# Revit family: 1001R
name_source: partatom
category: Plumbing Fixtures
revit_build: Autodesk Revit 2018 (Build: 20170223_1515(x64)
units: mm (PartAtom-declared; Revit-internal decimal feet)

## family parameters
Cut with Voids When Loaded = No
Host = Face
OmniClass Number = 23.45.05.21.11.11
OmniClass Title = Water Operated Water Closets
Part Type = Normal
Room Calculation Point = No
Round Connector Dimension = Use Diameter
Shared = Yes

## types (1)
- 1001R
    1001R Rear-Mounted Toilet, Wall Supply = Yes
    Amperage = 0
    Assembly Code = D2010110
    CW Connection = Yes
    CWFU = 10
    Default Elevation = 15"
    Description = Wall Hung Toilet, Rear Mount
    EG Enviro-Glaze (for color selection see flier) = No
    HW Connection = Yes
    HWFU = 0
    Inlet Water Diameter = 1 1/2"
    Inlet Water Radius = 3/4"
    Installation Type = Wall Mounted
    Length = 24 1/4"
    Manufacturer = Murdock
    Material = Metal Murdock 304 Stainless Steel
    Model = 1001R
    Product Documentation Link = https://www.murdockmfg.com
    Product Page URL = https://www.murdockmfg.com
    Tempered Water Connection = No
    Toilet Waste wall Outlet Diameter = 2 3/8"
    Toilet Waste wall Outlet Radius = 1 3/16"
    URL = https://www.murdockmfg.com
    Vent Connection = No
    Voltage = 0
    WFU = 10
    Wall Supply Flush Valve = Yes
    Warranty Documentation Link = https://www.murdockmfg.com
    Waste Connection = Yes
    Width = 14"

## geometry (parser evidence)
native form markers: Sweep x3
no freeform markers — native parametric forms only
